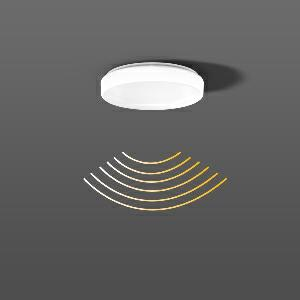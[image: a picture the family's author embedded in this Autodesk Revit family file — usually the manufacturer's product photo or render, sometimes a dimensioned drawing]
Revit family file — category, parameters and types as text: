
# Revit family: flat_polymero_kreis_slim_312084_002_2_191_a826
name_source: partatom
category: Lighting Fixtures
units: mm (PartAtom-declared; Revit-internal decimal feet)

## family parameters
Cut with Voids When Loaded = No
Host = Face
Light Source = No
Part Type = Normal
Room Calculation Point = No
Round Connector Dimension = Use Diameter
Shared = No

## types (1)
- FLAT POLYMERO KREIS SLIM (1 x LED Modul 830, 1300 lm, 3000)
    Apparent Load = 13 VA
    CIE Flux Codes = 43 73 92 88 100
    Color Rendering = 80
    Color Temperature = 3000
    Default Elevation = 1800 mm
    Description = Series: FLAT POLYMERO KREIS SLIM
Flat decorative round LED surface-mounted luminaire. Base: metal, powder-coated. Diffuser made of plastic (polycarbonate), opal, shockproof. Diffuser fastening: patented push system. Suitable for Ceiling mounting, Wall (surface). Slave luminaire. Can only be operated in combination with corresponding master luminaire. 
Colour: white
Diameter: 300 mm
Height: 65 mm
Lamp: LED exchangeable
Socket: without socket
Colour temperature: 3000K
Colour rendering index (CRI): 83
System power: 13 W
Rated luminous flux: 1300 lm
Luminous efficiency: 100 lm/W
Control gear: Converter not necessary
Protection class: I
Type of protection: IP 40
    Height = 65 mm
    Lamp = 1 x LED Modul 830
    Lamp Light Flux = 1300 lm
    Lamp count = 1
    Length = 300 mm
    Lifetime = 50000 h
    Luminous efficacy = 100 lm/W
    Manufacturer = RZB
    ModVariant = No
    Model = 312084.002.2.191
    Mounting Place = Ceiling, Wall
    Mounting Type = Surface mounted
    Number of Poles = 1
    OnlyDefault = Yes
    Power Factor = 1
    Product Name = FLAT POLYMERO KREIS SLIM
    Product group = Surface mounted ceiling and wall luminaires
    ProductGroupID = 305
    Protection Class = Protection class I
    Protection Degree = IP 40
    RLX_Detail_Level = 1
    RLX_Emergency_Light_Flux = 0 lm
    RLX_Emergency_Type = 0
    RLX_Emergency_Type_DB = No
    RlxData = <blob elided: 70169 chars, md5=1ec35527>
    Socket = socket
    Standby Power = 0 W
    System Light Flux = 1300 lm
    System Power = 13 W
    Type Comments = Product without accessories
    Type Image = 312084.002.1.19.jpg
    URL = http://relux.com
    VarID = ---
    Voltage = 230 V
    Voltage Range = 220-240 V
    Weight = 0.00 kg
    Width = 0 mm  [stored 0 ft]

note: [stored X ft] marks values corroborated as IEEE doubles in the binary element streams (Revit-internal decimal feet)

## geometry (parser evidence)
native form markers: Blend x4, Sweep x12
no freeform markers — native parametric forms only
